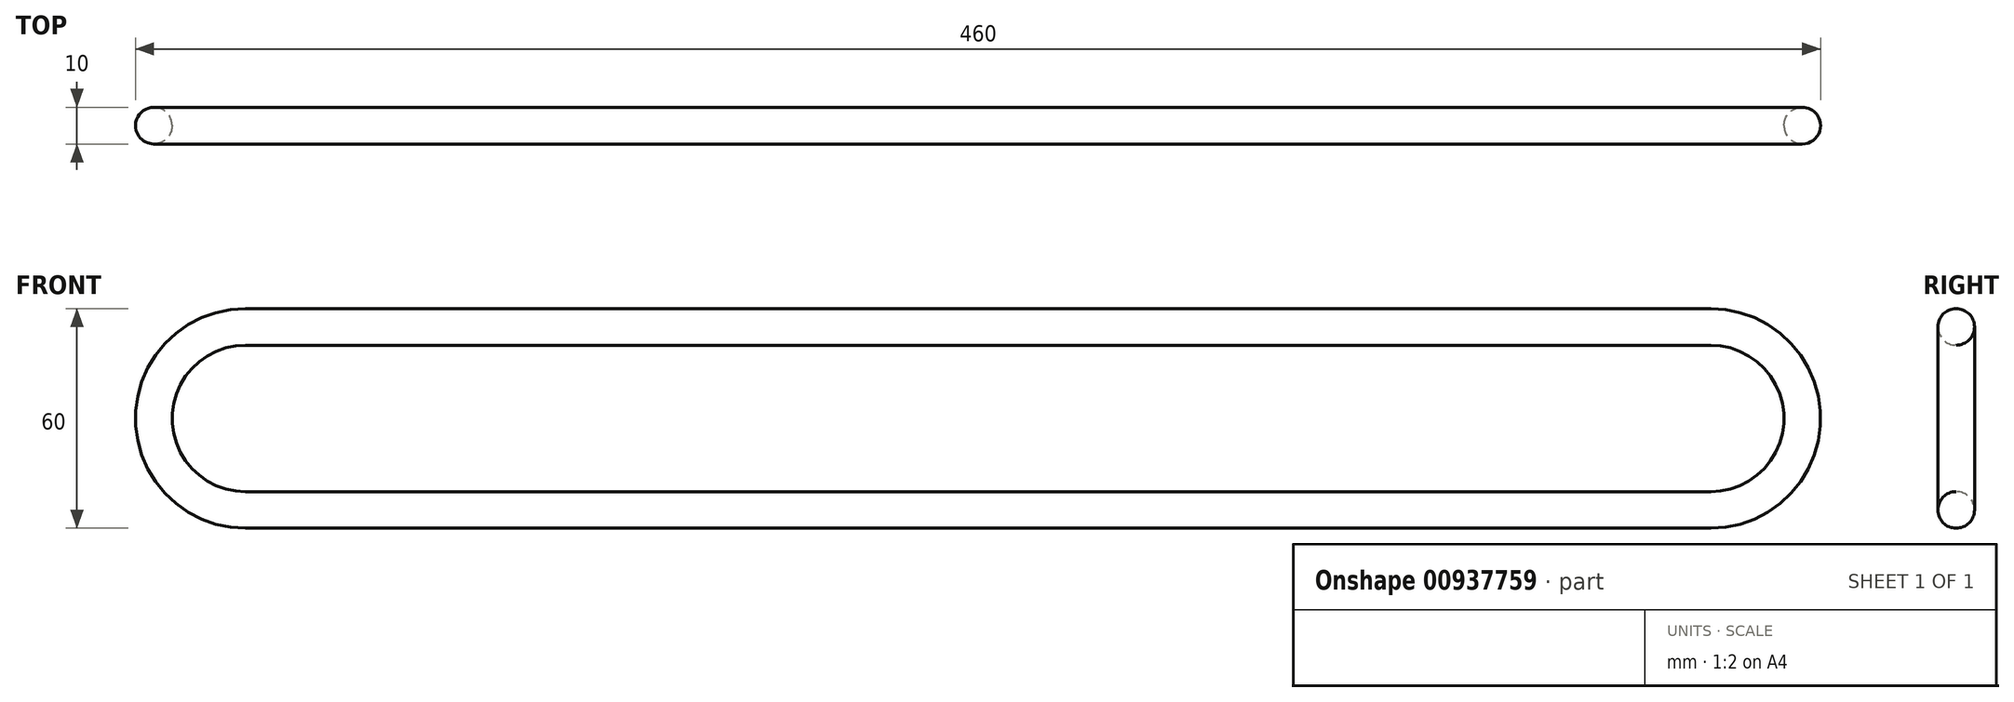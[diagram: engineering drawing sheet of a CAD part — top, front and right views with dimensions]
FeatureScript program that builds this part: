
annotation { "Feature Type Name" : "Feature", "Feature Type Description" : "" }
export const myFeature = defineFeature(function(context is Context, id is Id, definition is map)
    precondition{}
    {
        {
            var Q0;
            Q0=qCreatedBy(makeId("Front.planeOp"),FACE);
            var sketch = newSketch(context, id + "F0", { "sketchPlane" : qUnion([Q0])});
            skArc(sketch, "E0", {"start": v(-200, 25) * mm, "mid": v(-225, 0) * mm, "end": v(-200, -25) * mm});
            skArc(sketch, "E1", {"start": v(200, -25) * mm, "mid": v(225, 0) * mm, "end": v(200, 25) * mm});
            skLineSegment(sketch, "E2", {"start": v(-200, 25) * mm, "end": v(200, 25) * mm});
            skLineSegment(sketch, "E3", {"start": v(200, -25) * mm, "end": v(-200, -25) * mm});
            skSolve(sketch);
        }
        {
            var Q0;
            Q0=qCreatedBy(makeId("Right.planeOp"),FACE);
            var sketch = newSketch(context, id + "F1", { "sketchPlane" : qUnion([Q0])});
            skPoint(sketch, "E4", {"position": v(0, 25) * mm});
            skCircle(sketch, "E5", {"center": v(0, 25) * mm, "radius": 5 * mm});
            skSolve(sketch);
        }
        {
            var Q0;
            Q0=makeQuery(id+"F1.imprint","IMPRINT",FACE,{"disambiguationData":[TD([[makeQuery(id+"F1.imprint","IMPRINT",EDGE,{"derivedFrom":sQuery(id+"F1.wireOp",EDGE,"E5")}),1.0]])]});
            var Q1;
            Q1=sQuery(id+"F0.wireOp",EDGE,"E2");
            var Q2;
            Q2=sQuery(id+"F0.wireOp",EDGE,"E0");
            var Q3;
            Q3=sQuery(id+"F0.wireOp",EDGE,"E3");
            var Q4;
            Q4=sQuery(id+"F0.wireOp",EDGE,"E1");
            sweep(context, id + "F2", {"profiles" : qUnion([Q0]), "path" : qUnion([Q1, Q2, Q3, Q4])});
        }
    });
